# Revit family: Cypher-C1
name_source: partatom
category: Lighting Fixtures
revit_build: Autodesk Revit 2013 (Build: 20130531_2115(x64)
units: mm (PartAtom-declared; Revit-internal decimal feet)

## types (6) — shared parameters
120 Voltage = Yes
277 Voltage = No
Assembly Code = D5020
Box Finish = Hubbell-White
Color Filter = 16777215
Description = Cypher allows designers to mix and match optics for best-in-class aesthetics and performance
Dimming Lamp Color Temperature Shift = <None>
Emit Shape Visible in Rendering = No
Emit from Rectangle Length = 2 "
Emit from Rectangle Width = 4 "
Glass = Hubbell-White Glass
Lamp = 360° Light Distribution
Load Classification = Lighting
Manufacturer = Architectural Area Lighting
Manufacturer Fax = 626-369-2695
Model = Cypher - Accent Scale
Photometric Notes = More IES files download Photometric Web Link
Photometric Web Link = http://www.aal.net
Power Factor = 1
Product Documentation Link = http://www.aal.net
Product Page URL = http://www.aal.net
Tilt Angle = 90.00°
URL = http://www.aal.net
Voltage = 120 V

## per-type parameters (varying)
| type | Apparent Load | Photometric Web File | Wattage Comments | Watts |
| CY1-15-3K7-1-1D-R | 17 VA | CY1-15-3K7-1-1D-R.IES | 15W, 1500 nominal lumens | 17 W |
| CY1-15-4K7-1-WG-R | 17 VA | CY1-15-4K7-1-WG-R.IES | 15W, 1500 nominal lumens | 17 W |
| CY1-15-5K7-1-3D-R | 17 VA | CY1-15-5K7-1-3D-R.IES | 15W, 1500 nominal lumens | 17 W |
| CY1-25-3K7-1-1-R | 26 VA | CY1-25-3K7-1-1-R.IES | 25W, 2500 nominal lumens | 26 W |
| CY1-25-4K7-1-4-R | 26 VA | CY1-25-4K7-1-4-R.IES | 25W, 2500 nominal lumens | 26 W |
| CY1-25-5K7-1-SP-R | 26 VA | CY1-25-5K7-1-SP-R.IES | 25W, 2500 nominal lumens | 26 W |

## geometry (parser evidence)
native form markers: Blend x32, Sweep x3
no freeform markers — native parametric forms only
